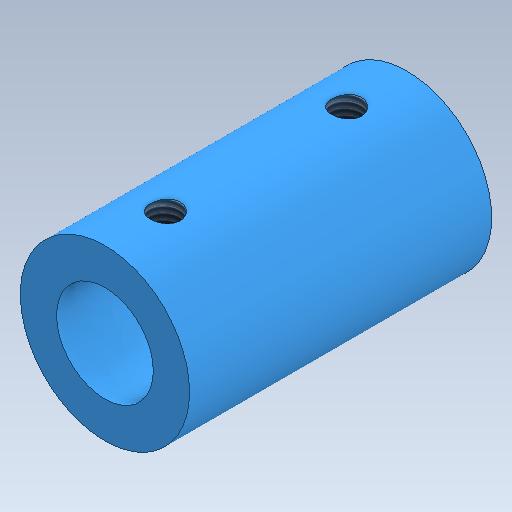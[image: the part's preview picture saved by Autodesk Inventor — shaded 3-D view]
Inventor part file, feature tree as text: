
AUTODESK INVENTOR PART (.ipt)
format: ipt  version: 2020 (Build 240168000, 168)  size: 143,360 bytes
history: native  units: mm
features: sketch x3, hole x2, extrude x1
ambient origin geometry x8: Origin, YZ Plane, XZ Plane, XY Plane, X Axis, Y Axis, Z Axis, Center Point
bodies: Solid1 (feature_tree)
feature tree (6):
  extrude  "Extrusion1"  Depth=25.0mm TaperAngle=0.0deg
  hole  "Hole1"  [1 undecoded]
  hole  "Hole2"  [1 undecoded]
  sketch  "Sketch1"  dims[d0=14.0mm d1=25.0mm d2=0.0mm]
  sketch  "Sketch3"  dims[d3=5.0mm d4=6.0mm d5=8.0mm d6=12.5mm d7=90.0deg d8=8.0mm d9=20.594885mm d10=5.0mm]
  sketch  "Sketch4"  dims[d11=5.0mm d12=2.459mm d13=8.0mm d14=8.0mm d15=12.5mm d16=90.0deg d17=8.8mm d18=20.594885mm]
note: 2 required parameter values undecoded (feature->parameter linkage not recoverable at this tier; creation-order binding heuristic only, values carry confidence <= 0.55)
